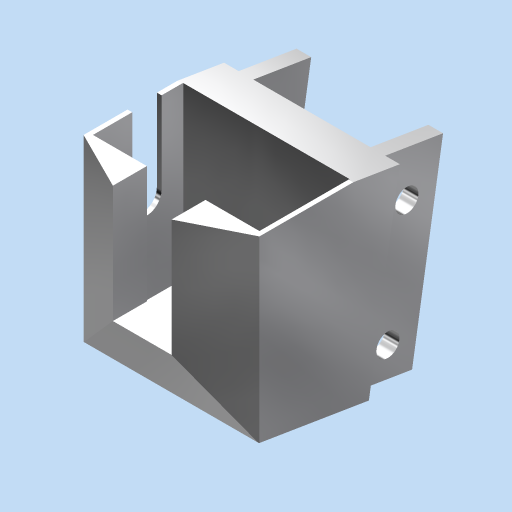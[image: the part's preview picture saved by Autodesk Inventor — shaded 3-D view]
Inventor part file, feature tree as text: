
AUTODESK INVENTOR PART (.ipt)
format: ipt  version: 2024 (Build 280153000, 153)  size: 524,288 bytes
history: native  units: in
note: dims shown in document units (in); Inventor stores cm internally (conversion verified against a paired STEP export)
features: extrude x14, sketch x14, chamfer x3, plane x3, other x3, projected_geometry x3, thicken_offset x1
ambient origin geometry x2: Origin, Center Point
bodies: Solid1 (feature_tree)
feature tree (41):
  extrude  "Extrusion1"  Depth=0.5in
  extrude  "Extrusion2"  Depth=0.8in
  extrude  "Extrusion3"  Depth=0.125in TaperAngle=0.0deg
  extrude  "Extrusion4"  Depth=0.125in TaperAngle=0.0deg
  extrude  "Extrusion5"  Depth=0.05in
  extrude  "Extrusion6"  Depth=1.45in TaperAngle=0.0deg
  extrude  "Extrusion7"  Depth=0.45in TaperAngle=0.0deg
  extrude  "Extrusion8"  Depth=0.45in TaperAngle=0.0deg
  extrude  "Extrusion9"  Depth=0.45in TaperAngle=0.0deg
  extrude  "Extrusion10"  Depth=0.25in
  thicken_offset  "Thicken1"
  extrude  "Extrusion11"  Depth=0.25in TaperAngle=45.0deg
  chamfer  "Chamfer1"  Distance=0.25in Angle=45.0deg
  chamfer  "Chamfer2"  Distance=0.25in Angle=45.0deg
  chamfer  "Chamfer3"  Distance=1.0in
  extrude  "Extrusion12"  Depth=2.0in TaperAngle=0.0deg
  extrude  "Extrusion13"  Depth=0.5in TaperAngle=0.0deg
  extrude  "Extrusion14"  [1 undecoded]
  plane  "YZ Plane Vertical Spine"
  plane  "XZ Plane Horizontal"
  plane  "XY Plane Vertical Span"
  other  "X Axis Left/Right"
  other  "Y Axis Up/Down"
  other  "Z Axis Fore/Aft"
  sketch  "Sketch1"  dims[d6=0.125in d7=0.0in d11=0.5in]
  sketch  "Sketch2"  dims[d13=0.196in d14=0.8in]
  sketch  "Sketch3"  dims[d16=1.0in d17=0.0in d18=0.125in d19=0.0in]
  sketch  "Sketch4"  dims[d20=0.125in d21=0.0in d22=0.125in d23=0.0in]
  projected_geometry  "Projected Loop1"
  sketch  "Sketch5"  dims[d24=0.05in d25=0.05in]
  sketch  "Sketch6"  dims[d26=0.05in d27=1.45in d28=0.0in]
  sketch  "Sketch7"  dims[d29=0.05in d30=0.45in d31=0.0in]
  sketch  "Sketch8"  dims[d32=0.05in d33=0.45in d34=0.0in]
  sketch  "Sketch9"  dims[d35=0.45in d36=0.0in d37=2.0in d38=0.0in]
  sketch  "Sketch10"  dims[d39=0.25in d40=0.25in]
  sketch  "Sketch11"  dims[d41=2.0in d42=0.0in d43=0.25in d44=0.5in d45=45.0deg d46=0.25in d47=0.5in d48=45.0deg d49=0.25in d50=0.485in d51=45.0deg d55=1.0in d56=0.0in]
  sketch  "Sketch13"  dims[d57=0.01in d58=2.0in d59=0.0in]
  sketch  "Sketch14"  dims[d60=0.5in d61=2.0in d62=0.0in]
  projected_geometry  "Projected Loop2"
  sketch  "Sketch15"
  projected_geometry  "Projected Loop3"
note: 1 required parameter value undecoded (feature->parameter linkage not recoverable at this tier; creation-order binding heuristic only, values carry confidence <= 0.55)
